# Revit family: Shower-Showerhead_Handshower_Set-KOHLER-ELEVATION-K-11827T_1
name_source: partatom
category: Plumbing Fixtures
revit_build: Autodesk Revit 2017 (Build: 20160225_1515(x64)
units: mm (PartAtom-declared; Revit-internal decimal feet)

## family parameters
Cut with Voids When Loaded = No
Host = Face
OmniClass Number = 23.31.17.00
OmniClass Title = Showers
Part Type = Normal
Room Calculation Point = No
Round Connector Dimension = Use Diameter
Shared = No

## types (2) — shared parameters
ADA Compliant = No
Assembly Code = D2010700
CW Connection = Yes
Cold Water Inlet = Cold Water Inlet
Date Modified = 04/27/2021
Default Elevation = 42"
Description = WM SHOWER/W CURVED SHWR COLUMN
Drain Included = No
Finish = Kohler-Metal-CP-Polished_Chrome
Flow Rate = 0 GPM
HW Connection = Yes
Height = 47 1/8"
Hot Water Inlet = Hot Water Inlet
Length = 20 7/8"
Manufacturer = KOHLER Co.
Master Format 2014 = 22 42 23
Master Format 2014 Name = Residential Showers
Material = Premium Metal Construction
Pressure = 72.52 psi
Product Name = Elevation
URL = http://www.kohler.com.cn
Vent Connection = No
Waste Connection = No
Waste Water Outlet = Waste Water Outlet
WaterSense Certified = No
Width = 5 15/16"

## per-type parameters (varying)
| type | Model | Type |
| 7, CP-Polished Chrome | K-11827T-7-CP | 1 |
| C7, CP-Polished Chrome | K-11827T-C7-CP | 2 |

## geometry (parser evidence)
native form markers: Sweep x5
no freeform markers — native parametric forms only
